# Revit family: Door-Internal-Single_Flush-Hollow_Meta_Drywall
name_source: partatom
category: Doors
revit_build: Autodesk Revit Architecture 2012 (Build: 20110916_2132(x64)
units: mm (PartAtom-declared; Revit-internal decimal feet)

## types (60) — shared parameters
Current_version = 1
Door Handle Height = 3' - 9"
Door Material = Metal_Gray_Galvanized_Satin
Fire Resistance = 1 hour
Frame Material = Metal_Gray_Galvanized_Satin
Function = Interior
Glass Material = Glass_Green-Blue
Handle Material = Metal_Chrome_Satin
Life Expectancy = -
Link to website = -
Louver Material = Metal_Gray_Galvanized_Satin
Manufacturer Details = -
No Fly Zone = Yes
No Fly Zone Material = No Fly Zone
Powered_by = http://bimservice.com.ua
Soffit Width = 0' - 3"
Swing Angle = 25.00°
Thickness = 0' - 1 3/4"
TypeName = HONEYCOMB CORE DOOR
Uniclass = -
Wall Closure = By host
Warranty = 5 years

## per-type parameters (varying)
| type | Door Panel Hight | Door Panel Width | Double Rabbet | Glazing Height | Glazing Width | Height | Louver Width | NominalHeight | NominalWidth | Panel G | Panel L | Single Rabbet | Width |
| 4'-0"x8'-0"_DblFrame_L | 7' - 11 27/32" | 3' - 11 13/16" | Yes | 3' - 11" | 3' - 0" | 8' - 0" | 3' - 0" | 8' - 0" | 4' - 0" | No | Yes | No | 4' - 0" |
| 4'-0"x7'-0"_DblFrame_L | 6' - 11 27/32" | 3' - 11 13/16" | Yes | 2' - 11" | 3' - 0" | 7' - 0" | 3' - 0" | 7' - 0" | 4' - 0" | No | Yes | No | 4' - 0" |
| 4'-0"x6'-8"_DblFrame_L | 6' - 7 27/32" | 3' - 11 13/16" | Yes | 2' - 7" | 3' - 0" | 6' - 8" | 3' - 0" | 6' - 8" | 4' - 0" | No | Yes | No | 4' - 0" |
| 4'-0"x8'-0"_SnglFrame_L | 7' - 11 27/32" | 3' - 11 13/16" | No | 3' - 11" | 3' - 0" | 8' - 0" | 3' - 0" | 8' - 0" | 4' - 0" | No | Yes | Yes | 4' - 0" |
| 4'-0"x7'-0"_SnglFrame_L | 6' - 11 27/32" | 3' - 11 13/16" | No | 2' - 11" | 3' - 0" | 7' - 0" | 3' - 0" | 7' - 0" | 4' - 0" | No | Yes | Yes | 4' - 0" |
| 4'-0"x6'-8"_SnglFrame_L | 6' - 7 27/32" | 3' - 11 13/16" | No | 2' - 7" | 3' - 0" | 6' - 8" | 3' - 0" | 6' - 8" | 4' - 0" | No | Yes | Yes | 4' - 0" |
| 3'-6"x8'-0"_DblFrame_L | 7' - 11 27/32" | 3' - 5 13/16" | Yes | 3' - 11" | 2' - 6" | 8' - 0" | 2' - 6" | 8' - 0" | 3' - 6" | No | Yes | No | 3' - 6" |
| 3'-6"x7'-0"_DblFrame_L | 6' - 11 27/32" | 3' - 5 13/16" | Yes | 2' - 11" | 2' - 6" | 7' - 0" | 2' - 6" | 7' - 0" | 3' - 6" | No | Yes | No | 3' - 6" |
| 3'-6"x6'-8"_DblFrame_L | 6' - 7 27/32" | 3' - 5 13/16" | Yes | 2' - 7" | 2' - 6" | 6' - 8" | 2' - 6" | 6' - 8" | 3' - 6" | No | Yes | No | 3' - 6" |
| 3'-6"x8'-0"_SnglFrame_L | 7' - 11 27/32" | 3' - 5 13/16" | No | 3' - 11" | 2' - 6" | 8' - 0" | 2' - 6" | 8' - 0" | 3' - 6" | No | Yes | Yes | 3' - 6" |
| 3'-6"x7'-0"_SnglFrame_L | 6' - 11 27/32" | 3' - 5 13/16" | No | 2' - 11" | 2' - 6" | 7' - 0" | 2' - 6" | 7' - 0" | 3' - 6" | No | Yes | Yes | 3' - 6" |
| 3'-6"x6'-8"_SnglFrame_L | 6' - 7 27/32" | 3' - 5 13/16" | No | 2' - 7" | 2' - 6" | 6' - 8" | 2' - 6" | 6' - 8" | 3' - 6" | No | Yes | Yes | 3' - 6" |
| 3'-0"x8'-0"_DblFrame_L | 7' - 11 27/32" | 2' - 11 13/16" | Yes | 3' - 11" | 2' - 0" | 8' - 0" | 2' - 0" | 8' - 0" | 3' - 0" | No | Yes | No | 3' - 0" |
| 3'-0"x7'-0"_DblFrame_L | 6' - 11 27/32" | 2' - 11 13/16" | Yes | 2' - 11" | 2' - 0" | 7' - 0" | 2' - 0" | 7' - 0" | 3' - 0" | No | Yes | No | 3' - 0" |
| 3'-0"x6'-8"_DblFrame_L | 6' - 7 27/32" | 2' - 11 13/16" | Yes | 2' - 7" | 2' - 0" | 6' - 8" | 2' - 0" | 6' - 8" | 3' - 0" | No | Yes | No | 3' - 0" |
| 3'-0"x8'-0"_SnglFrame_L | 7' - 11 27/32" | 2' - 11 13/16" | No | 3' - 11" | 2' - 0" | 8' - 0" | 2' - 0" | 8' - 0" | 3' - 0" | No | Yes | Yes | 3' - 0" |
| 3'-0"x7'-0"_SnglFrame_L | 6' - 11 27/32" | 2' - 11 13/16" | No | 2' - 11" | 2' - 0" | 7' - 0" | 2' - 0" | 7' - 0" | 3' - 0" | No | Yes | Yes | 3' - 0" |
| 3'-0"x6'-8"_SnglFrame_L | 6' - 7 27/32" | 2' - 11 13/16" | No | 2' - 7" | 2' - 0" | 6' - 8" | 2' - 0" | 6' - 8" | 3' - 0" | No | Yes | Yes | 3' - 0" |
| 2'-8"x8'-0"_DblFrame_L | 7' - 11 27/32" | 2' - 7 13/16" | Yes | 3' - 11" | 1' - 8" | 8' - 0" | 1' - 8" | 8' - 0" | 2' - 8" | No | Yes | No | 2' - 8" |
| 2'-8"x7'-0"_DblFrame_L | 6' - 11 27/32" | 2' - 7 13/16" | Yes | 2' - 11" | 1' - 8" | 7' - 0" | 1' - 8" | 7' - 0" | 2' - 8" | No | Yes | No | 2' - 8" |
| 2'-8"x6'-8"_DblFrame_L | 6' - 7 27/32" | 2' - 7 13/16" | Yes | 2' - 7" | 1' - 8" | 6' - 8" | 1' - 8" | 6' - 8" | 2' - 8" | No | Yes | No | 2' - 8" |
| 2'-8"x8'-0"_SnglFrame_L | 7' - 11 27/32" | 2' - 7 13/16" | No | 3' - 11" | 1' - 8" | 8' - 0" | 1' - 8" | 8' - 0" | 2' - 8" | No | Yes | Yes | 2' - 8" |
| 2'-8"x7'-0"_SnglFrame_L | 6' - 11 27/32" | 2' - 7 13/16" | No | 2' - 11" | 1' - 8" | 7' - 0" | 1' - 8" | 7' - 0" | 2' - 8" | No | Yes | Yes | 2' - 8" |
| 2'-8"x6'-8"_SnglFrame_L | 6' - 7 27/32" | 2' - 7 13/16" | No | 2' - 7" | 1' - 8" | 6' - 8" | 1' - 8" | 6' - 8" | 2' - 8" | No | Yes | Yes | 2' - 8" |
| 2'-6"x8'-0"_DblFrame_L | 7' - 11 27/32" | 2' - 5 13/16" | Yes | 3' - 11" | 1' - 6" | 8' - 0" | 1' - 6" | 8' - 0" | 2' - 6" | No | Yes | No | 2' - 6" |
| 2'-6"x7'-0"_DblFrame_L | 6' - 11 27/32" | 2' - 5 13/16" | Yes | 2' - 11" | 1' - 6" | 7' - 0" | 1' - 6" | 7' - 0" | 2' - 6" | No | Yes | No | 2' - 6" |
| 2'-6"x6'-8"_DblFrame_L | 6' - 7 27/32" | 2' - 5 13/16" | Yes | 2' - 7" | 1' - 6" | 6' - 8" | 1' - 6" | 6' - 8" | 2' - 6" | No | Yes | No | 2' - 6" |
| 2'-6"x8'-0"_SnglFrame_L | 7' - 11 27/32" | 2' - 5 13/16" | No | 3' - 11" | 1' - 6" | 8' - 0" | 1' - 6" | 8' - 0" | 2' - 6" | No | Yes | Yes | 2' - 6" |
| 2'-6"x7'-0"_SnglFrame_L | 6' - 11 27/32" | 2' - 5 13/16" | No | 2' - 11" | 1' - 6" | 7' - 0" | 1' - 6" | 7' - 0" | 2' - 6" | No | Yes | Yes | 2' - 6" |
| 2'-6"x6'-8"_SnglFrame_L | 6' - 7 27/32" | 2' - 5 13/16" | No | 2' - 7" | 1' - 6" | 6' - 8" | 1' - 6" | 6' - 8" | 2' - 6" | No | Yes | Yes | 2' - 6" |
| 4'-0"x8'-0"_DblFrame_G | 7' - 11 27/32" | 3' - 11 13/16" | Yes | 3' - 11" | 3' - 0" | 8' - 0" | 3' - 0" | 8' - 0" | 4' - 0" | Yes | No | No | 4' - 0" |
| 4'-0"x7'-0"_DblFrame_G | 6' - 11 27/32" | 3' - 11 13/16" | Yes | 2' - 11" | 3' - 0" | 7' - 0" | 3' - 0" | 7' - 0" | 4' - 0" | Yes | No | No | 4' - 0" |
| 4'-0"x6'-8"_DblFrame_G | 6' - 7 27/32" | 3' - 11 13/16" | Yes | 2' - 7" | 3' - 0" | 6' - 8" | 3' - 0" | 6' - 8" | 4' - 0" | Yes | No | No | 4' - 0" |
| 4'-0"x8'-0"_SnglFrame_G | 7' - 11 27/32" | 3' - 11 13/16" | No | 3' - 11" | 3' - 0" | 8' - 0" | 3' - 0" | 8' - 0" | 4' - 0" | Yes | No | Yes | 4' - 0" |
| 4'-0"x7'-0"_SnglFrame_G | 6' - 11 27/32" | 3' - 11 13/16" | No | 2' - 11" | 3' - 0" | 7' - 0" | 3' - 0" | 7' - 0" | 4' - 0" | Yes | No | Yes | 4' - 0" |
| 4'-0"x6'-8"_SnglFrame_G | 6' - 7 27/32" | 3' - 11 13/16" | No | 2' - 7" | 3' - 0" | 6' - 8" | 3' - 0" | 6' - 8" | 4' - 0" | Yes | No | Yes | 4' - 0" |
| 3'-6"x8'-0"_DblFrame_G | 7' - 11 27/32" | 3' - 5 13/16" | Yes | 3' - 11" | 2' - 6" | 8' - 0" | 2' - 6" | 8' - 0" | 3' - 6" | Yes | No | No | 3' - 6" |
| 3'-6"x7'-0"_DblFrame_G | 6' - 11 27/32" | 3' - 5 13/16" | Yes | 2' - 11" | 2' - 6" | 7' - 0" | 2' - 6" | 7' - 0" | 3' - 6" | Yes | No | No | 3' - 6" |
| 3'-6"x6'-8"_DblFrame_G | 6' - 7 27/32" | 3' - 5 13/16" | Yes | 2' - 7" | 2' - 6" | 6' - 8" | 2' - 6" | 6' - 8" | 3' - 6" | Yes | No | No | 3' - 6" |
| 3'-6"x8'-0"_SnglFrame_G | 7' - 11 27/32" | 3' - 5 13/16" | No | 3' - 11" | 2' - 6" | 8' - 0" | 2' - 6" | 8' - 0" | 3' - 6" | Yes | No | Yes | 3' - 6" |
| 3'-6"x7'-0"_SnglFrame_G | 6' - 11 27/32" | 3' - 5 13/16" | No | 2' - 11" | 2' - 6" | 7' - 0" | 2' - 6" | 7' - 0" | 3' - 6" | Yes | No | Yes | 3' - 6" |
| 3'-6"x6'-8"_SnglFrame_G | 6' - 7 27/32" | 3' - 5 13/16" | No | 2' - 7" | 2' - 6" | 6' - 8" | 2' - 6" | 6' - 8" | 3' - 6" | Yes | No | Yes | 3' - 6" |
| 3'-0"x8'-0"_DblFrame_G | 7' - 11 27/32" | 2' - 11 13/16" | Yes | 3' - 11" | 2' - 0" | 8' - 0" | 2' - 0" | 8' - 0" | 3' - 0" | Yes | No | No | 3' - 0" |
| 3'-0"x7'-0"_DblFrame_G | 6' - 11 27/32" | 2' - 11 13/16" | Yes | 2' - 11" | 2' - 0" | 7' - 0" | 2' - 0" | 7' - 0" | 3' - 0" | Yes | No | No | 3' - 0" |
| 3'-0"x6'-8"_DblFrame_G | 6' - 7 27/32" | 2' - 11 13/16" | Yes | 2' - 7" | 2' - 0" | 6' - 8" | 2' - 0" | 6' - 8" | 3' - 0" | Yes | No | No | 3' - 0" |
| 3'-0"x8'-0"_SnglFrame_G | 7' - 11 27/32" | 2' - 11 13/16" | No | 3' - 11" | 2' - 0" | 8' - 0" | 2' - 0" | 8' - 0" | 3' - 0" | Yes | No | Yes | 3' - 0" |
| 3'-0"x7'-0"_SnglFrame_G | 6' - 11 27/32" | 2' - 11 13/16" | No | 2' - 11" | 2' - 0" | 7' - 0" | 2' - 0" | 7' - 0" | 3' - 0" | Yes | No | Yes | 3' - 0" |
| 3'-0"x6'-8"_SnglFrame_G | 6' - 7 27/32" | 2' - 11 13/16" | No | 2' - 7" | 2' - 0" | 6' - 8" | 2' - 0" | 6' - 8" | 3' - 0" | Yes | No | Yes | 3' - 0" |
| 2'-8"x8'-0"_DblFrame_G | 7' - 11 27/32" | 2' - 7 13/16" | Yes | 3' - 11" | 1' - 8" | 8' - 0" | 1' - 8" | 8' - 0" | 2' - 8" | Yes | No | No | 2' - 8" |
| 2'-8"x7'-0"_DblFrame_G | 6' - 11 27/32" | 2' - 7 13/16" | Yes | 2' - 11" | 1' - 8" | 7' - 0" | 1' - 8" | 7' - 0" | 2' - 8" | Yes | No | No | 2' - 8" |
| 2'-8"x6'-8"_DblFrame_G | 6' - 7 27/32" | 2' - 7 13/16" | Yes | 2' - 7" | 1' - 8" | 6' - 8" | 1' - 8" | 6' - 8" | 2' - 8" | Yes | No | No | 2' - 8" |
| 2'-8"x8'-0"_SnglFrame_G | 7' - 11 27/32" | 2' - 7 13/16" | No | 3' - 11" | 1' - 8" | 8' - 0" | 1' - 8" | 8' - 0" | 2' - 8" | Yes | No | Yes | 2' - 8" |
| 2'-8"x7'-0"_SnglFrame_G | 6' - 11 27/32" | 2' - 7 13/16" | No | 2' - 11" | 1' - 8" | 7' - 0" | 1' - 8" | 7' - 0" | 2' - 8" | Yes | No | Yes | 2' - 8" |
| 2'-8"x6'-8"_SnglFrame_G | 6' - 7 27/32" | 2' - 7 13/16" | No | 2' - 7" | 1' - 8" | 6' - 8" | 1' - 8" | 6' - 8" | 2' - 8" | Yes | No | Yes | 2' - 8" |
| 2'-6"x8'-0"_DblFrame_G | 7' - 11 27/32" | 2' - 5 13/16" | Yes | 3' - 11" | 1' - 6" | 8' - 0" | 1' - 6" | 8' - 0" | 2' - 6" | Yes | No | No | 2' - 6" |
| 2'-6"x7'-0"_DblFrame_G | 6' - 11 27/32" | 2' - 5 13/16" | Yes | 2' - 11" | 1' - 6" | 7' - 0" | 1' - 6" | 7' - 0" | 2' - 6" | Yes | No | No | 2' - 6" |
| 2'-6"x6'-8"_DblFrame_G | 6' - 7 27/32" | 2' - 5 13/16" | Yes | 2' - 7" | 1' - 6" | 6' - 8" | 1' - 6" | 6' - 8" | 2' - 6" | Yes | No | No | 2' - 6" |
| 2'-6"x8'-0"_SnglFrame_G | 7' - 11 27/32" | 2' - 5 13/16" | No | 3' - 11" | 1' - 6" | 8' - 0" | 1' - 6" | 8' - 0" | 2' - 6" | Yes | No | Yes | 2' - 6" |
| 2'-6"x7'-0"_SnglFrame_G | 6' - 11 27/32" | 2' - 5 13/16" | No | 2' - 11" | 1' - 6" | 7' - 0" | 1' - 6" | 7' - 0" | 2' - 6" | Yes | No | Yes | 2' - 6" |
| 2'-6"x6'-8"_SnglFrame_G | 6' - 7 27/32" | 2' - 5 13/16" | No | 2' - 7" | 1' - 6" | 6' - 8" | 1' - 6" | 6' - 8" | 2' - 6" | Yes | No | Yes | 2' - 6" |

## geometry (parser evidence)
native form markers: Blend x2, Sweep x24
no freeform markers — native parametric forms only
